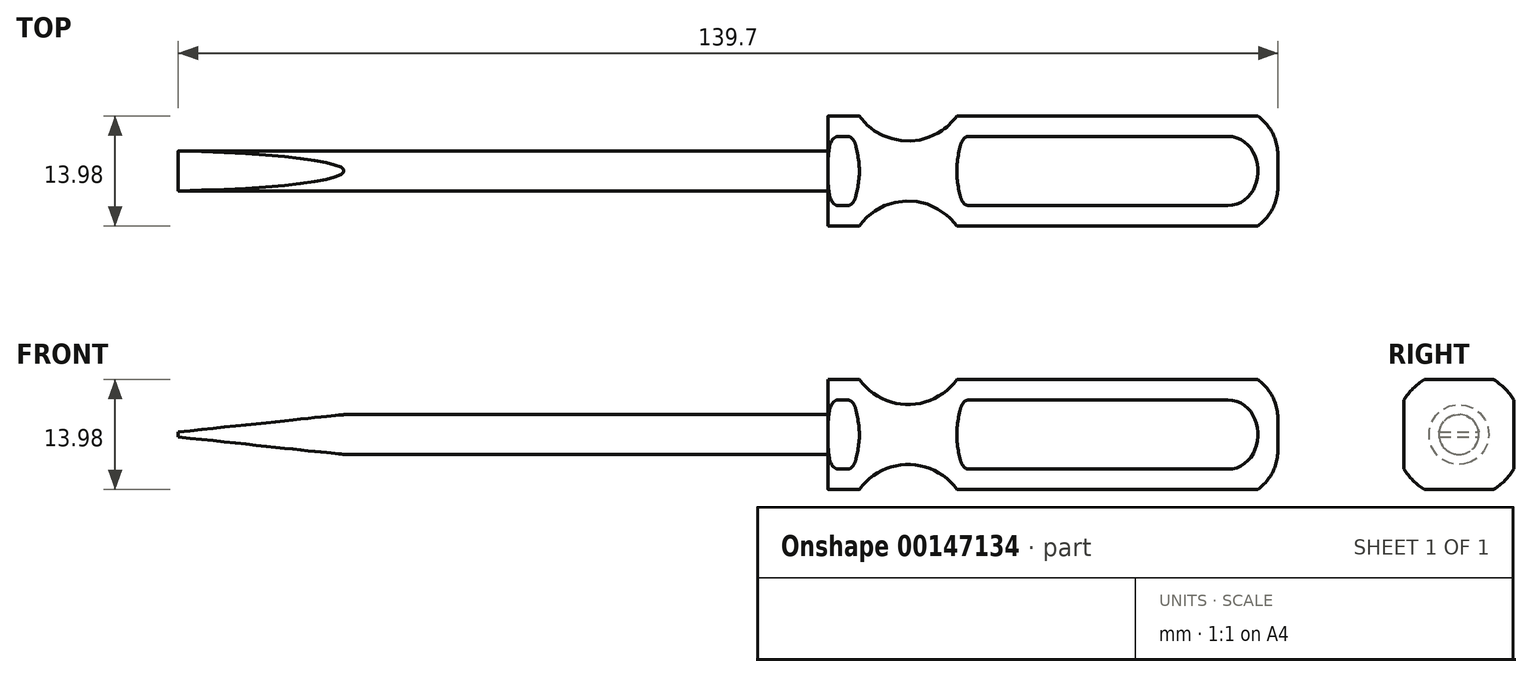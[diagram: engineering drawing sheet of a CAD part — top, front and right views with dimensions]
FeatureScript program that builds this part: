
annotation { "Feature Type Name" : "Feature", "Feature Type Description" : "" }
export const myFeature = defineFeature(function(context is Context, id is Id, definition is map)
    precondition{}
    {
        {
            var Q0;
            Q0=qCreatedBy(makeId("Front.planeOp"),FACE);
            var sketch = newSketch(context, id + "F0", { "sketchPlane" : qUnion([Q0])});
            skLineSegment(sketch, "E0", {"start": v(213.15, 0) * mm, "end": v(-149.72, 0) * mm, "construction": true});
            skLineSegment(sketch, "E1", {"start": v(0, 0) * mm, "end": v(-139.7, 0) * mm});
            skLineSegment(sketch, "E2", {"start": v(-139.7, 0) * mm, "end": v(-139.7, 2.54) * mm});
            skLineSegment(sketch, "E3", {"start": v(0, 0) * mm, "end": v(0, 1.9) * mm});
            skLineSegment(sketch, "E4", {"start": v(-139.7, 2.54) * mm, "end": v(-57.15, 2.54) * mm});
            skArc(sketch, "E5", {"start": v(-53.59, 7.62) * mm, "mid": v(-47, 3.81) * mm, "end": v(-40.4, 7.62) * mm});
            skLineSegment(sketch, "E6", {"start": v(-6.35, 8.26) * mm, "end": v(-39.3, 8.26) * mm});
            skLineSegment(sketch, "E7", {"start": v(-57.15, 6.98) * mm, "end": v(-57.15, 2.54) * mm});
            skLineSegment(sketch, "E8.trimOffspring", {"start": v(-54.69, 8.26) * mm, "end": v(-55.88, 8.26) * mm});
            skPoint(sketch, "E9.visualSharp", {"position": v(-57.15, 8.26) * mm});
            skArc(sketch, "E9.filletArc", {"start": v(-55.88, 8.25) * mm, "mid": v(-56.78, 7.88) * mm, "end": v(-57.15, 6.98) * mm});
            skPoint(sketch, "E10.visualSharp", {"position": v(-53.92, 8.26) * mm});
            skArc(sketch, "E10.filletArc", {"start": v(-53.59, 7.62) * mm, "mid": v(-54.05, 8.08) * mm, "end": v(-54.69, 8.26) * mm});
            skPoint(sketch, "E11.visualSharp", {"position": v(-40.06, 8.26) * mm});
            skArc(sketch, "E11.filletArc", {"start": v(-39.3, 8.26) * mm, "mid": v(-39.93, 8.08) * mm, "end": v(-40.4, 7.62) * mm});
            skPoint(sketch, "E12.visualSharp", {"position": v(0, 8.26) * mm});
            skArc(sketch, "E12.filletArc", {"start": v(0, 1.9) * mm, "mid": v(-1.86, 6.4) * mm, "end": v(-6.35, 8.26) * mm});
            skSolve(sketch);
        }
        {
            var Q0;
            Q0=makeQuery(id+"F0.imprint","IMPRINT",FACE,{"disambiguationData":[TD([[makeQuery(id+"F0.imprint","IMPRINT",EDGE,{"derivedFrom":sQuery(id+"F0.wireOp",EDGE,"E1")}),-1.0]])]});
            var Q1;
            Q1=sQuery(id+"F0.wireOp",EDGE,"E0");
            revolve(context, id + "F1", {"entities" : qUnion([Q0]), "axis" : qUnion([Q1]), "revolveType" : RevolveType.FULL});
        }
        {
            var Q0;
            Q0=qCreatedBy(makeId("Front.planeOp"),FACE);
            var sketch = newSketch(context, id + "F2", { "sketchPlane" : qUnion([Q0])});
            skLineSegment(sketch, "E13", {"start": v(0, 0) * mm, "end": v(-151.92, 0) * mm, "construction": true});
            skLineSegment(sketch, "E14", {"start": v(-139.7, 0.32) * mm, "end": v(-118.55, 2.54) * mm});
            skLineSegment(sketch, "E15", {"start": v(-139.7, 2.54) * mm, "end": v(-118.55, 2.54) * mm});
            skLineSegment(sketch, "E16.0", {"start": v(-139.7, 2.54) * mm, "end": v(-139.7, 0.32) * mm});
            skLineSegment(sketch, "E17.filletArc", {"start": v(-118.55, 2.54) * mm, "end": v(-118.55, 2.54) * mm});
            skPoint(sketch, "E18.newPointB", {"position": v(-139.7, -2.54) * mm});
            skLineSegment(sketch, "E18.filletArc", {"start": v(-139.7, 0.32) * mm, "end": v(-139.7, 0.32) * mm});
            skLineSegment(sketch, "E19.MirrorCS", {"start": v(-139.7, -2.54) * mm, "end": v(-118.55, -2.54) * mm});
            skLineSegment(sketch, "E20.MirrorCS", {"start": v(-139.7, -2.54) * mm, "end": v(-139.7, -0.32) * mm});
            skLineSegment(sketch, "E21.MirrorCS", {"start": v(-139.7, -0.32) * mm, "end": v(-118.55, -2.54) * mm});
            skSolve(sketch);
        }
        {
            var Q0;
            Q0=qCreatedBy(makeId("Right.planeOp"),FACE);
            var sketch = newSketch(context, id + "F3", { "sketchPlane" : qUnion([Q0])});
            skLineSegment(sketch, "E22", {"start": v(10.31, 0) * mm, "end": v(-10.18, 0) * mm, "construction": true});
            skLineSegment(sketch, "E23", {"start": v(0, 9.47) * mm, "end": v(0, -9.37) * mm, "construction": true});
            skLineSegment(sketch, "E24", {"start": v(6.99, 6.35) * mm, "end": v(6.99, -6.35) * mm});
            skLineSegment(sketch, "E25.0", {"start": v(8.83, 6.35) * mm, "end": v(8.83, -6.35) * mm});
            skLineSegment(sketch, "E26", {"start": v(6.99, 6.35) * mm, "end": v(8.83, 6.35) * mm});
            skLineSegment(sketch, "E27", {"start": v(6.99, -6.35) * mm, "end": v(8.83, -6.35) * mm});
            skLineSegment(sketch, "E28.1.0", {"start": v(-6.35, 6.99) * mm, "end": v(6.35, 6.99) * mm});
            skLineSegment(sketch, "E28.1.1", {"start": v(6.35, 6.99) * mm, "end": v(6.35, 8.83) * mm});
            skLineSegment(sketch, "E28.1.2", {"start": v(-6.35, 8.83) * mm, "end": v(6.35, 8.83) * mm});
            skLineSegment(sketch, "E28.1.3", {"start": v(-6.35, 6.99) * mm, "end": v(-6.35, 8.83) * mm});
            skLineSegment(sketch, "E28.2.0", {"start": v(-6.99, -6.35) * mm, "end": v(-6.99, 6.35) * mm});
            skLineSegment(sketch, "E28.2.1", {"start": v(-6.99, 6.35) * mm, "end": v(-8.83, 6.35) * mm});
            skLineSegment(sketch, "E28.2.2", {"start": v(-8.83, -6.35) * mm, "end": v(-8.83, 6.35) * mm});
            skLineSegment(sketch, "E28.2.3", {"start": v(-6.99, -6.35) * mm, "end": v(-8.83, -6.35) * mm});
            skLineSegment(sketch, "E28.3.0", {"start": v(6.35, -6.99) * mm, "end": v(-6.35, -6.99) * mm});
            skLineSegment(sketch, "E28.3.1", {"start": v(-6.35, -6.99) * mm, "end": v(-6.35, -8.83) * mm});
            skLineSegment(sketch, "E28.3.2", {"start": v(6.35, -8.83) * mm, "end": v(-6.35, -8.83) * mm});
            skLineSegment(sketch, "E28.3.3", {"start": v(6.35, -6.99) * mm, "end": v(6.35, -8.83) * mm});
            skPoint(sketch, "E28.center", {"position": v(0, 0) * mm});
            skSolve(sketch);
        }
        {
            var Q0;
            Q0 = qSketchRegion(id + "F3", true);
            var Q1;
            Q1=makeQuery(id+"F1.opRevolve","SWEPT_FACE",FACE,{"disambiguationData":[OSD([sQuery(id+"F0.wireOp",EDGE,"E7")])]});
            extrude(context, id + "F4", {"entities" : qUnion([Q0, Q1]), "operationType" : NewBodyOperationType.REMOVE, "oppositeDirection" : true, "depth" : 59.88 * mm});
        }
        {
            var Q0;
            Q0 = qSketchRegion(id + "F2", true);
            extrude(context, id + "F5", {"entities" : qUnion([Q0]), "operationType" : NewBodyOperationType.REMOVE, "endBound" : BoundingType.SYMMETRIC, "depth" : 25.4 * mm});
        }
    });
